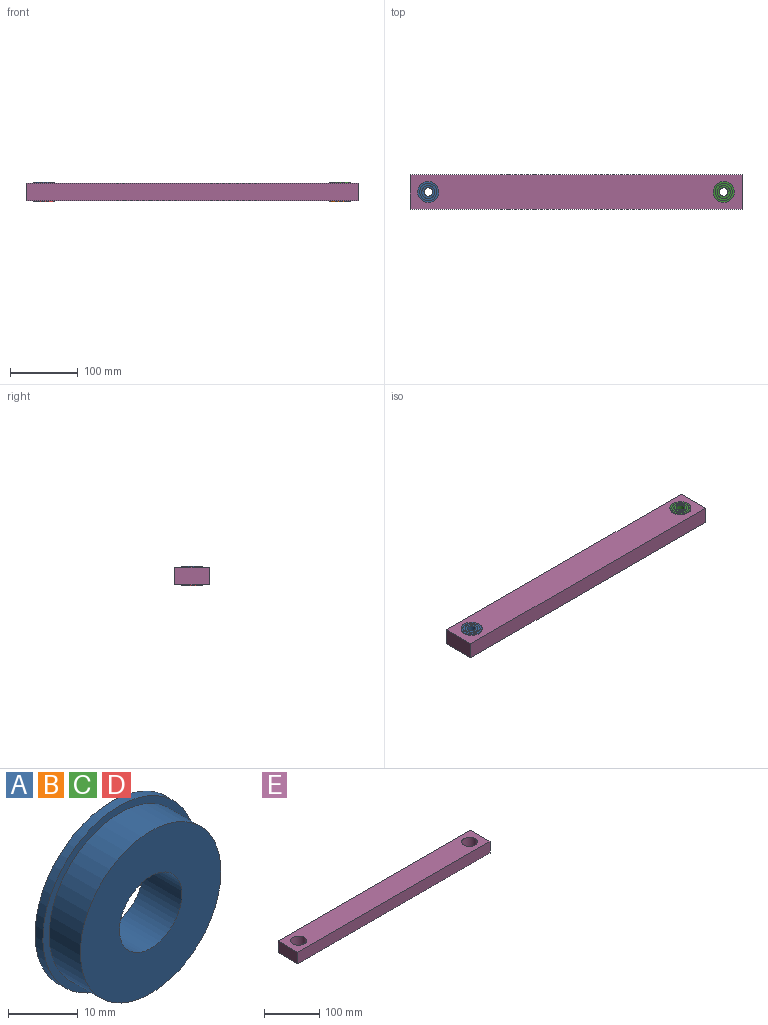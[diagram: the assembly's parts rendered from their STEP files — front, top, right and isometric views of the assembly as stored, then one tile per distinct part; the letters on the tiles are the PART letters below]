
ASSEMBLY  parts=5 mates=4
PART A: 10 faces, bbox 31.1x7.9x31.1 mm
  f0: cylinder r=12.7mm len=25.4mm, axis (0,1,0), area 30.4mm2, adj f8,f9
  f1: cylinder r=15.56mm len=31.12mm, axis (0,1,0), area 155.2mm2, adj f7,f8
  f2: cylinder r=14.29mm len=28.58mm, axis (0,1,0), area 570mm2, adj f6,f7
  f3: cylinder r=6.35mm len=12.7mm, axis (0,1,0), area 316.7mm2, adj f5,f6
  f4: cylinder r=9.53mm len=19.05mm, axis (0,1,0), area 22.8mm2, adj f5,f9
  f5: plane 19.05x19.05mm, normal (0,1,0), area 158.3mm2, adj f3,f4
  f6: plane 28.58x28.58mm, normal (0,-1,0), area 514.6mm2, adj f2,f3
  f7: plane 31.12x31.12mm, normal (0,-1,0), area 119.1mm2, adj f1,f2
  f8: plane 31.12x31.12mm, normal (0,1,0), area 253.7mm2, adj f0,f1
  f9: plane 25.4x25.4mm, normal (0,1,0), area 221.7mm2, adj f0,f4
PART B: same geometry as A
PART C: same geometry as A
PART D: same geometry as A
PART E: 8 faces, bbox 490x50.8x25.4 mm
  f0: plane 490.01x25.4mm, normal (0,1,0), area 12446.2mm2, adj f1,f5,f6,f7
  f1: plane 50.8x25.4mm, normal (-1,0,0), area 1290.3mm2, adj f0,f2,f6,f7
  f2: plane 490.01x25.4mm, normal (0,-1,0), area 12446.2mm2, adj f1,f5,f6,f7
  f3: cylinder r=14.29mm len=28.58mm, axis (0,0,-1), area 2280.2mm2, adj f6,f7
  f4: cylinder r=14.29mm len=28.58mm, axis (0,0,-1), area 2280.2mm2, adj f6,f7
  f5: plane 50.8x25.4mm, normal (1,0,0), area 1290.3mm2, adj f0,f2,f6,f7
  f6: plane 490.01x50.8mm, normal (0,0,1), area 23609.8mm2, adj f0,f1,f2,f3,f4,f5
  f7: plane 490.01x50.8mm, normal (0,0,-1), area 23609.8mm2, adj f0,f1,f2,f3,f4,f5
PLACE A rot(axis=(1,0,0),90deg) t=(-218.22,-28.18,-34.64)mm
PLACE B rot(axis=(-1,0,0),90deg) t=(217.81,-28.18,-47.34)mm
PLACE C rot(axis=(1,0,0),90deg) t=(217.81,-28.18,-34.64)mm
PLACE D rot(axis=(-1,0,0),90deg) t=(-218.22,-28.18,-47.34)mm
PLACE E t=(-163.67,-18.09,-53.69)mm
MATE revolute C.f0 <-> E.f4  axis (0,0,-1) through (217.81,-28.18,-28.29)mm
MATE fastened B.f0 <-> E.f4  axis (0,0,1) through (217.81,-28.18,-53.69)mm
MATE revolute A.f0 <-> E.f3  axis (0,0,-1) through (-218.22,-28.18,-28.29)mm
MATE fastened D.f0 <-> E.f3  axis (0,0,1) through (-218.22,-28.18,-53.69)mm
